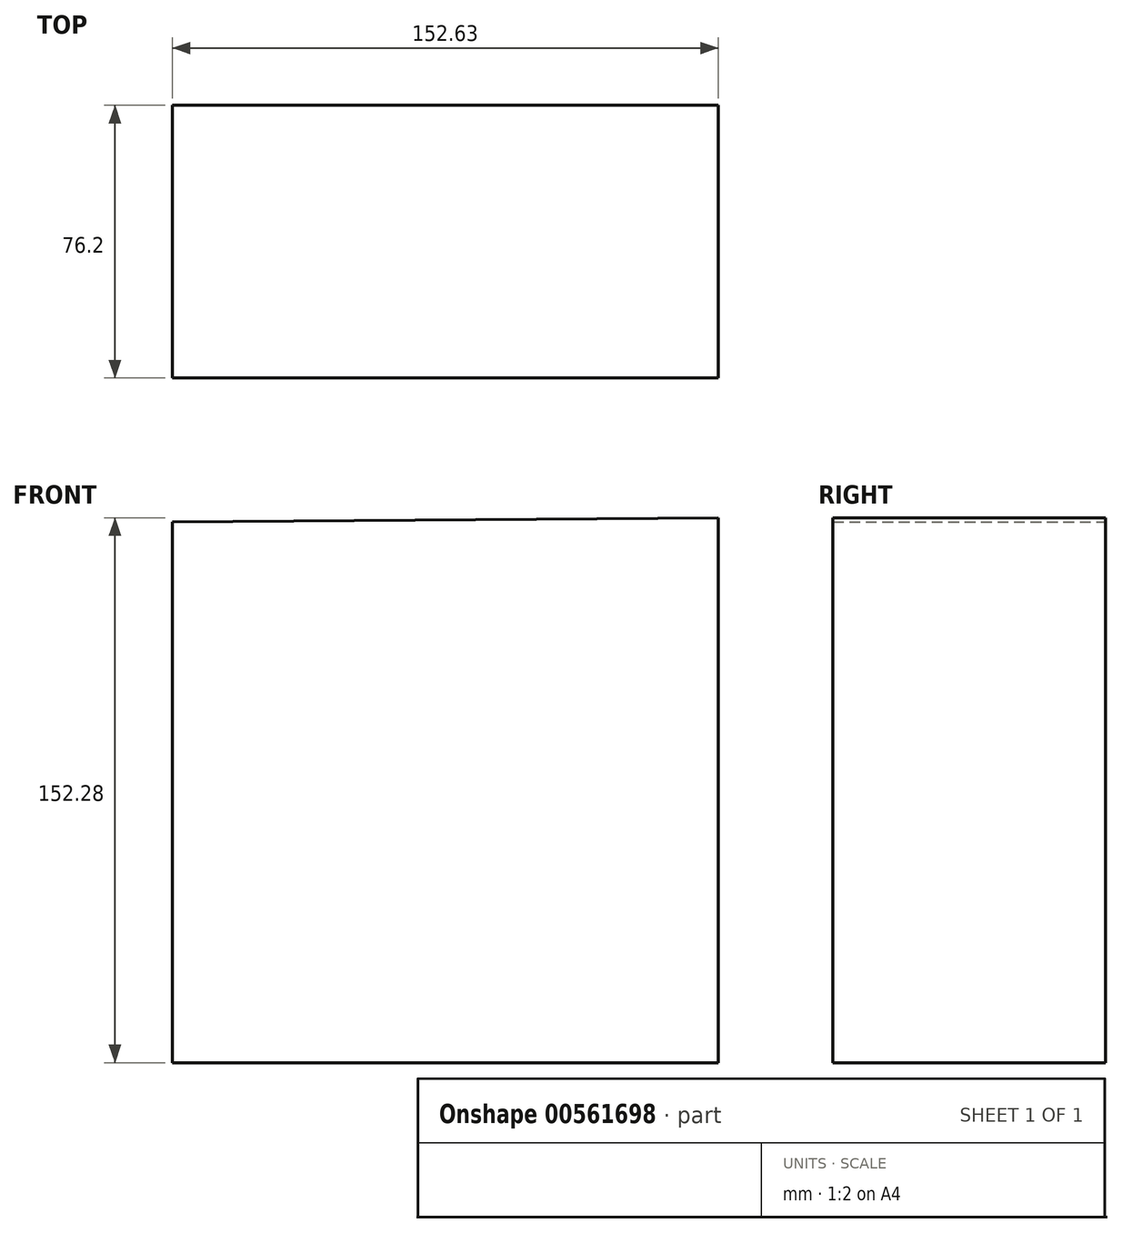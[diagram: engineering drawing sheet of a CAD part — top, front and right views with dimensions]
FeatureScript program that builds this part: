
annotation { "Feature Type Name" : "Feature", "Feature Type Description" : "" }
export const myFeature = defineFeature(function(context is Context, id is Id, definition is map)
    precondition{}
    {
        {
            var Q0;
            Q0=qCreatedBy(makeId("Front.planeOp"),FACE);
            var sketch = newSketch(context, id + "F0", { "sketchPlane" : qUnion([Q0])});
            skLineSegment(sketch, "E0", {"start": v(-76.29, 74.9) * mm, "end": v(-76.29, -76.22) * mm});
            skLineSegment(sketch, "E1", {"start": v(-76.29, -76.22) * mm, "end": v(76.34, -76.22) * mm});
            skLineSegment(sketch, "E2", {"start": v(76.34, -76.22) * mm, "end": v(76.34, 76.06) * mm});
            skLineSegment(sketch, "E3", {"start": v(76.34, 76.06) * mm, "end": v(-76.29, 74.9) * mm});
            skSolve(sketch);
        }
        {
            var Q0;
            Q0 = qSketchRegion(id + "F0", true);
            extrude(context, id + "F1", {"entities" : qUnion([Q0]), "depth" : 76.2 * mm, "offsetDistance" : 25.4 * mm});
        }
    });
